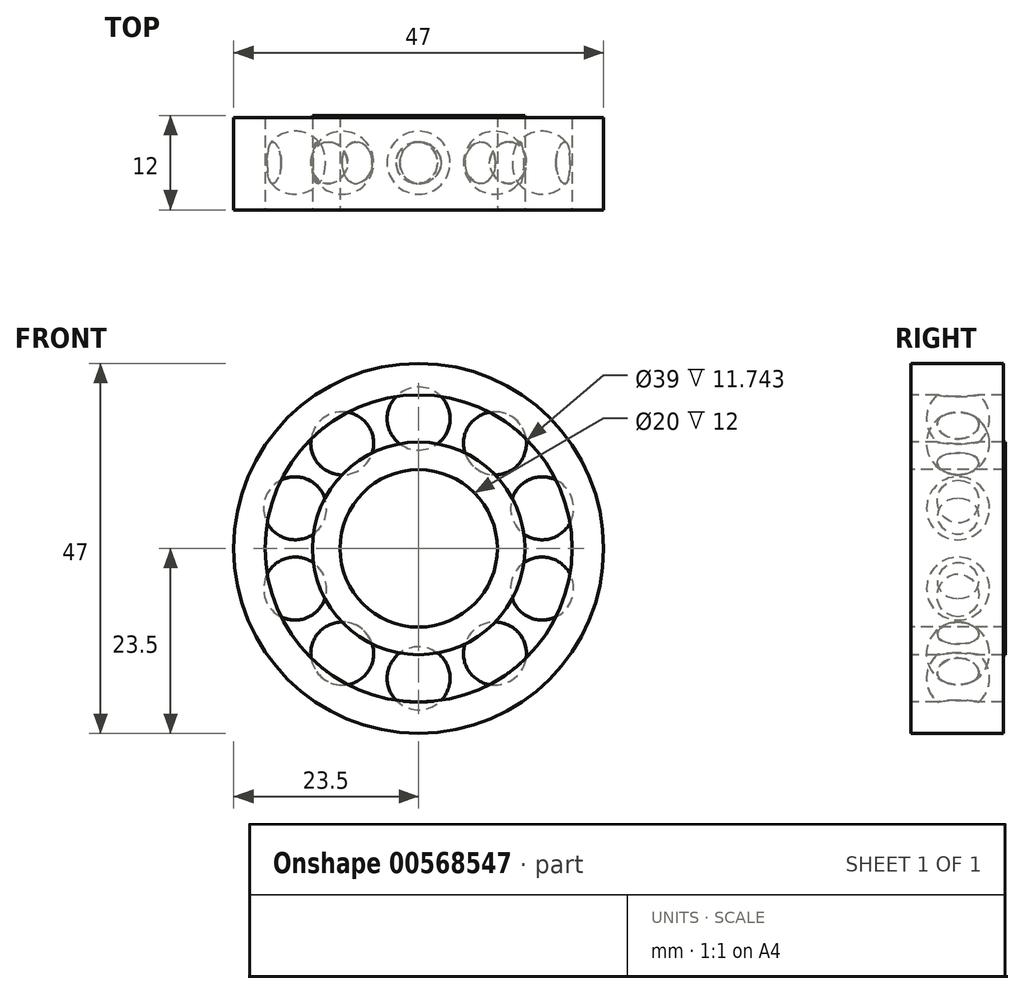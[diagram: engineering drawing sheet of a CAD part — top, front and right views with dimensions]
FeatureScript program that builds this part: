
annotation { "Feature Type Name" : "Feature", "Feature Type Description" : "" }
export const myFeature = defineFeature(function(context is Context, id is Id, definition is map)
    precondition{}
    {
        {
            var Q0;
            Q0=qCreatedBy(makeId("Right.planeOp"),FACE);
            var sketch = newSketch(context, id + "F0", { "sketchPlane" : qUnion([Q0])});
            skLineSegment(sketch, "E0.bottom", {"start": v(0, 23.5) * mm, "end": v(11.74, 23.5) * mm});
            skLineSegment(sketch, "E0.top", {"start": v(0, 19.5) * mm, "end": v(11.74, 19.5) * mm});
            skLineSegment(sketch, "E0.left", {"start": v(0, 23.5) * mm, "end": v(0, 19.5) * mm});
            skLineSegment(sketch, "E0.right", {"start": v(11.74, 23.5) * mm, "end": v(11.74, 19.5) * mm});
            skLineSegment(sketch, "E1.bottom", {"start": v(0, 13.5) * mm, "end": v(12, 13.5) * mm});
            skLineSegment(sketch, "E1.top", {"start": v(0, 10) * mm, "end": v(12, 10) * mm});
            skLineSegment(sketch, "E1.left", {"start": v(0, 13.5) * mm, "end": v(0, 10) * mm});
            skLineSegment(sketch, "E1.right", {"start": v(12, 13.5) * mm, "end": v(12, 10) * mm});
            skLineSegment(sketch, "E2", {"start": v(0, 0) * mm, "end": v(22.85, 0) * mm, "construction": true});
            skSolve(sketch);
        }
        {
            var Q0;
            Q0 = qSketchRegion(id + "F0", true);
            var Q1;
            Q1=sQuery(id+"F0.wireOp",EDGE,"E2");
            revolve(context, id + "F1", {"entities" : qUnion([Q0]), "axis" : qUnion([Q1]), "revolveType" : RevolveType.FULL});
        }
        {
            var Q0;
            Q0=qCreatedBy(makeId("Front.planeOp"),FACE);
            cPlane(context, id + "F2", {"entities" : qUnion([Q0]), "cplaneType" : CPlaneType.OFFSET, "offset" : 6 * mm, "oppositeDirection" : true, "width" : 150 * mm, "height" : 150 * mm});
        }
        {
            var Q0;
            Q0=qCreatedBy(id+"F2.planeOp",FACE);
            var sketch = newSketch(context, id + "F3", { "sketchPlane" : qUnion([Q0])});
            skArc(sketch, "E3", {"start": v(0, 12.5) * mm, "mid": v(4, 16.5) * mm, "end": v(0, 20.5) * mm});
            skLineSegment(sketch, "E4", {"start": v(0, 20.5) * mm, "end": v(0, 12.5) * mm});
            skPoint(sketch, "E5.orphan", {"position": v(0, 28.09) * mm});
            skSolve(sketch);
        }
        {
            var Q0;
            Q0=makeQuery(id+"F3.imprint","IMPRINT",FACE,{"disambiguationData":[TD([[makeQuery(id+"F3.imprint","IMPRINT",EDGE,{"derivedFrom":sQuery(id+"F3.wireOp",EDGE,"E3")}),1.0]])]});
            var Q1;
            Q1=sQuery(id+"F3.wireOp",EDGE,"E4");
            revolve(context, id + "F4", {"entities" : qUnion([Q0]), "axis" : qUnion([Q1]), "revolveType" : RevolveType.FULL});
        }
        {
            var Q0;
            Q0=makeQuery(id+"F4.opRevolve","SWEPT_BODY",BODY,{"disambiguationData":[OSD([sQuery(id+"F3.wireOp",EDGE,"E3"),sQuery(id+"F3.wireOp",EDGE,"E4")])]});
            var Q1;
            Q1=makeQuery(id+"F1.opRevolve","SWEPT_EDGE",EDGE,{"disambiguationData":[OSD([sQuery(id+"F0.wireOp",EDGE,"E0.bottom"),sQuery(id+"F0.wireOp",EDGE,"E0.left")])]});
            circularPattern(context, id + "F5", {"operationType" : NewBodyOperationType.ADD, "entities" : qUnion([Q0]), "axis" : qUnion([Q1]), "angle" : 360 * degree, "instanceCount" : 10, "equalSpace" : true});
        }
    });
